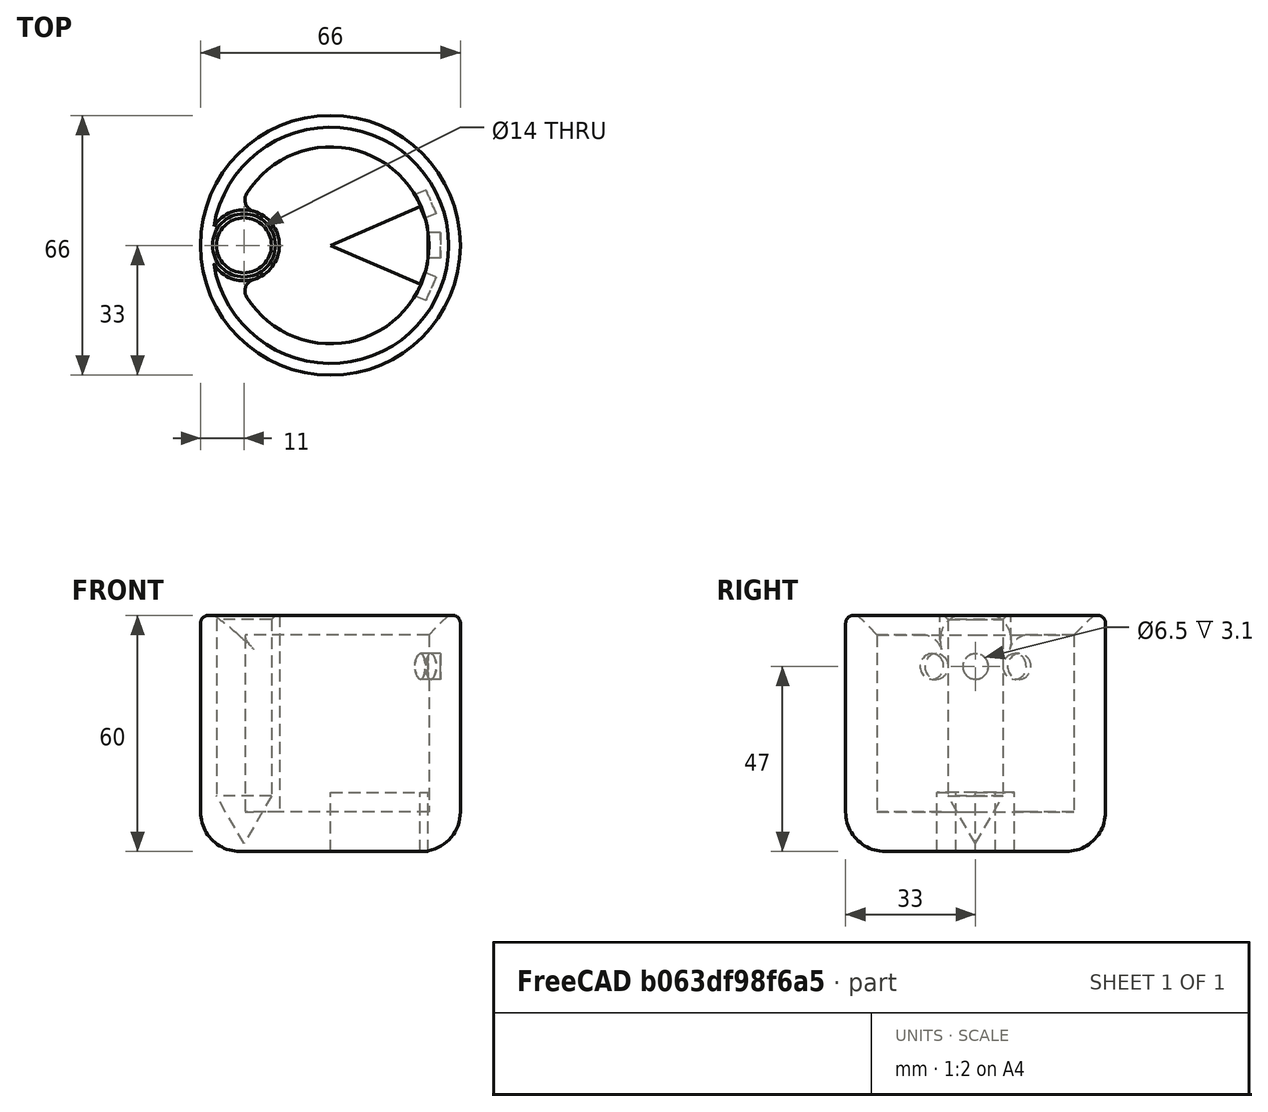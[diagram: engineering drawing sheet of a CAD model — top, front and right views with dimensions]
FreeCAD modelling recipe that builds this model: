
FCSTD DOCUMENT  (FreeCAD 0.17R13522 (Git))
Label: caddy4assembly
License: All rights reserved
LicenseURL: http://en.wikipedia.org/wiki/All_rights_reserved
objects: Part::Feature×5, Part::MultiFuse×1, Part::Cut×1
note: 7 computed .brp shape members not serialized (recipe doc carries the construction recipe); baked Part::Feature solids carry a one-line shape summary decoded from their .brp

FEATURE [Part::Feature] Body003  label="Cup001"
  shape: bbox 71.44 x 71.44 x 61.38 mm, 18 faces (baked)
FEATURE [Part::Feature] Body001001  label="Guide001"
  shape: bbox 24.8 x 19.73 x 15 mm, 7 faces (baked)
FEATURE [Part::Feature] Body002001  label="Magnet Hole001"
  Placement = pos=(24.8,0,15) rot=(-1,0,0;0.052905rad)
  shape: bbox 3.1 x 6.5 x 6.5 mm, 3 faces (baked)
FEATURE [Part::Feature] Body  label="Magnet Hole002"
  Placement = pos=(22.6852,-9.86379,15) rot=(0.634217,-0.131917,-0.761818;0.533071rad)
  shape: bbox 5.435 x 7.197 x 6.5 mm, 3 faces (baked)
FEATURE [Part::Feature] Body002002  label="Magnet Hole003"
  Placement = pos=(22.6852,9.86379,15) rot=(0.170381,0.035439,0.984741;0.416327rad)
  shape: bbox 5.435 x 7.197 x 6.5 mm, 3 faces (baked)
FEATURE [Part::MultiFuse] Fusion
  Placement = pos=(0,0,32) rot=(0,0,1;0rad)
  Shapes = -> [Body002002,Body,Body002001]
FEATURE [Part::Cut] Cut
  Base = -> Body003
  Tool = -> Fusion
